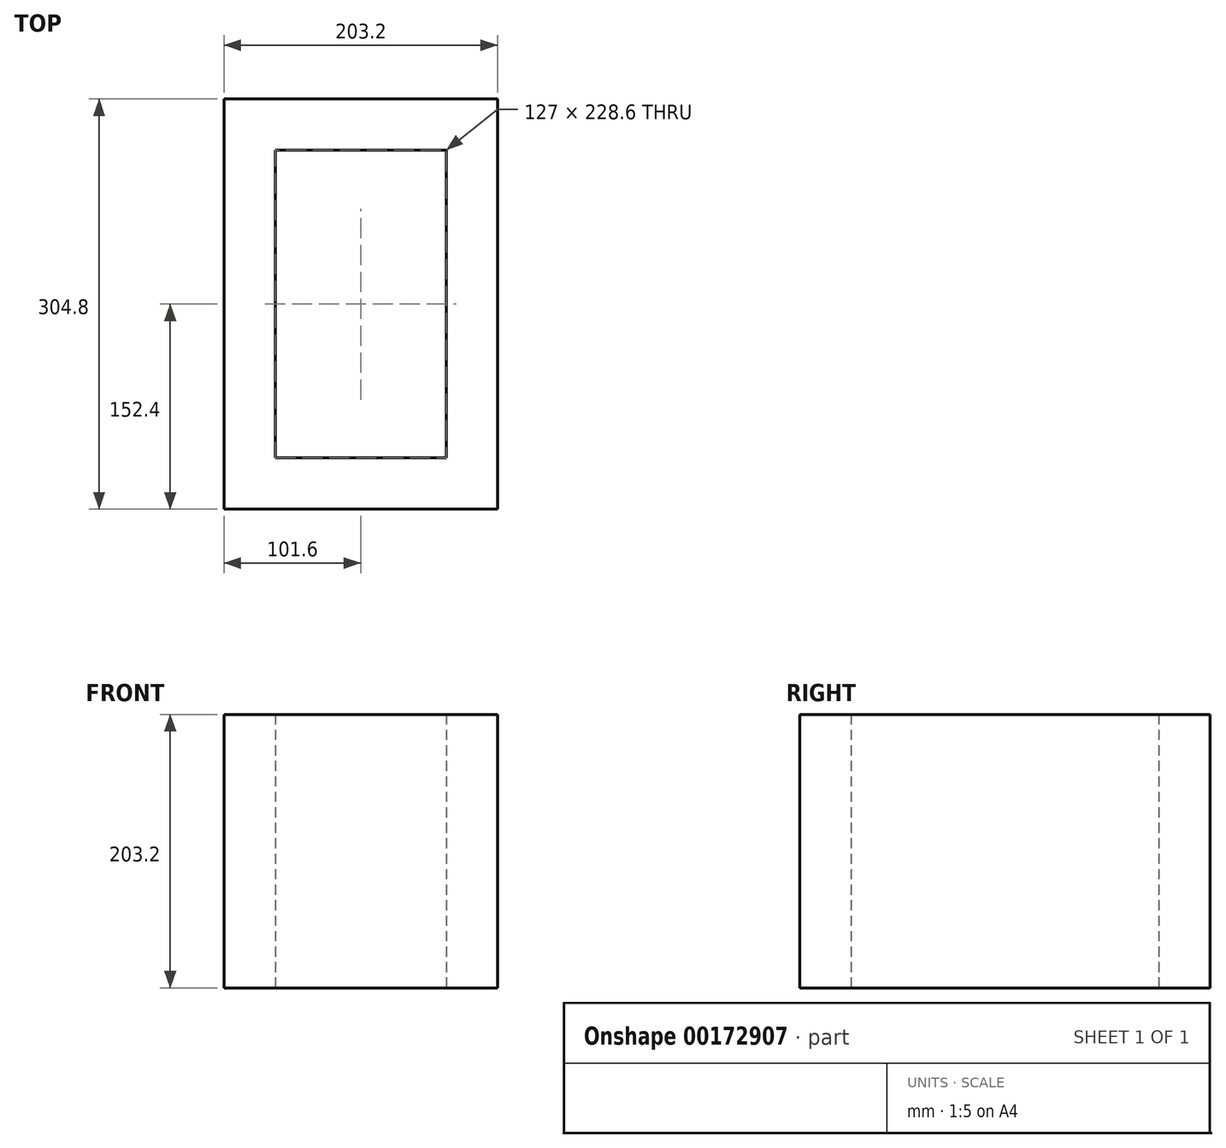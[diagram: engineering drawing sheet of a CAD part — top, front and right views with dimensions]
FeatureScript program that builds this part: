
annotation { "Feature Type Name" : "Feature", "Feature Type Description" : "" }
export const myFeature = defineFeature(function(context is Context, id is Id, definition is map)
    precondition{}
    {
        {
            var Q0;
            Q0=qCreatedBy(makeId("Front.planeOp"),FACE);
            var sketch = newSketch(context, id + "F0", { "sketchPlane" : qUnion([Q0])});
            skLineSegment(sketch, "E0.bottom", {"start": v(101.6, 101.6) * mm, "end": v(-101.6, 101.6) * mm});
            skLineSegment(sketch, "E0.top", {"start": v(101.6, -101.6) * mm, "end": v(-101.6, -101.6) * mm});
            skLineSegment(sketch, "E0.left", {"start": v(101.6, 101.6) * mm, "end": v(101.6, -101.6) * mm});
            skLineSegment(sketch, "E0.right", {"start": v(-101.6, 101.6) * mm, "end": v(-101.6, -101.6) * mm});
            skPoint(sketch, "E0.middle", {"position": v(0, 0) * mm});
            skSolve(sketch);
        }
        {
            var Q0;
            Q0=makeQuery(id+"F0.imprint","IMPRINT",FACE,{"disambiguationData":[TD([[makeQuery(id+"F0.imprint","IMPRINT",EDGE,{"derivedFrom":sQuery(id+"F0.wireOp",EDGE,"E0.bottom")}),1.0]])]});
            var Q1;
            Q1 = qSketchRegion(id + "F0", true);
            extrude(context, id + "F1", {"entities" : qUnion([Q0, Q1]), "oppositeDirection" : true, "depth" : 304.8 * mm});
        }
        {
            var Q0;
            Q0=makeQuery(id+"F1.opExtrude","SWEPT_FACE",FACE,{"disambiguationData":[OSD([sQuery(id+"F0.wireOp",EDGE,"E0.bottom")])]});
            var sketch = newSketch(context, id + "F2", { "sketchPlane" : qUnion([Q0])});
            skLineSegment(sketch, "E1.bottom", {"start": v(0, 304.8) * mm, "end": v(0, 304.8) * mm});
            skPoint(sketch, "E1.middle", {"position": v(0, 0) * mm});
            skLineSegment(sketch, "E2", {"start": v(-101.6, 0) * mm, "end": v(101.6, 304.8) * mm, "construction": true});
            skLineSegment(sketch, "E3", {"start": v(-101.6, 304.8) * mm, "end": v(101.6, 0) * mm, "construction": true});
            skPoint(sketch, "E4", {"position": v(0, 152.4) * mm});
            skLineSegment(sketch, "E5.bottom", {"start": v(-63.5, 266.7) * mm, "end": v(63.5, 266.7) * mm});
            skLineSegment(sketch, "E5.top", {"start": v(-63.5, 38.1) * mm, "end": v(63.5, 38.1) * mm});
            skLineSegment(sketch, "E5.left", {"start": v(-63.5, 266.7) * mm, "end": v(-63.5, 38.1) * mm});
            skLineSegment(sketch, "E5.right", {"start": v(63.5, 266.7) * mm, "end": v(63.5, 38.1) * mm});
            skPoint(sketch, "E6", {"position": v(-63.5, 152.4) * mm});
            skPoint(sketch, "E7", {"position": v(0, 38.1) * mm});
            skLineSegment(sketch, "E8", {"start": v(-63.5, 152.4) * mm, "end": v(-101.6, 152.4) * mm, "construction": true});
            skLineSegment(sketch, "E9", {"start": v(0, 38.1) * mm, "end": v(0, 0) * mm, "construction": true});
            skSolve(sketch);
        }
        {
            var Q0;
            Q0 = qSketchRegion(id + "F2", true);
            var Q1;
            Q1=makeQuery(id+"F1.opExtrude","SWEPT_FACE",FACE,{"disambiguationData":[OSD([sQuery(id+"F0.wireOp",EDGE,"E0.top")])]});
            extrude(context, id + "F3", {"entities" : qUnion([Q0]), "operationType" : NewBodyOperationType.REMOVE, "depth" : 25.4 * mm, "hasSecondDirection" : true, "secondDirectionBound" : SecondDirectionBoundingType.UP_TO_SURFACE, "secondDirectionOppositeDirection" : true, "secondDirectionBoundEntityFace" : qUnion([Q1]), "secondDirectionDepth" : 25.4 * mm});
        }
    });
